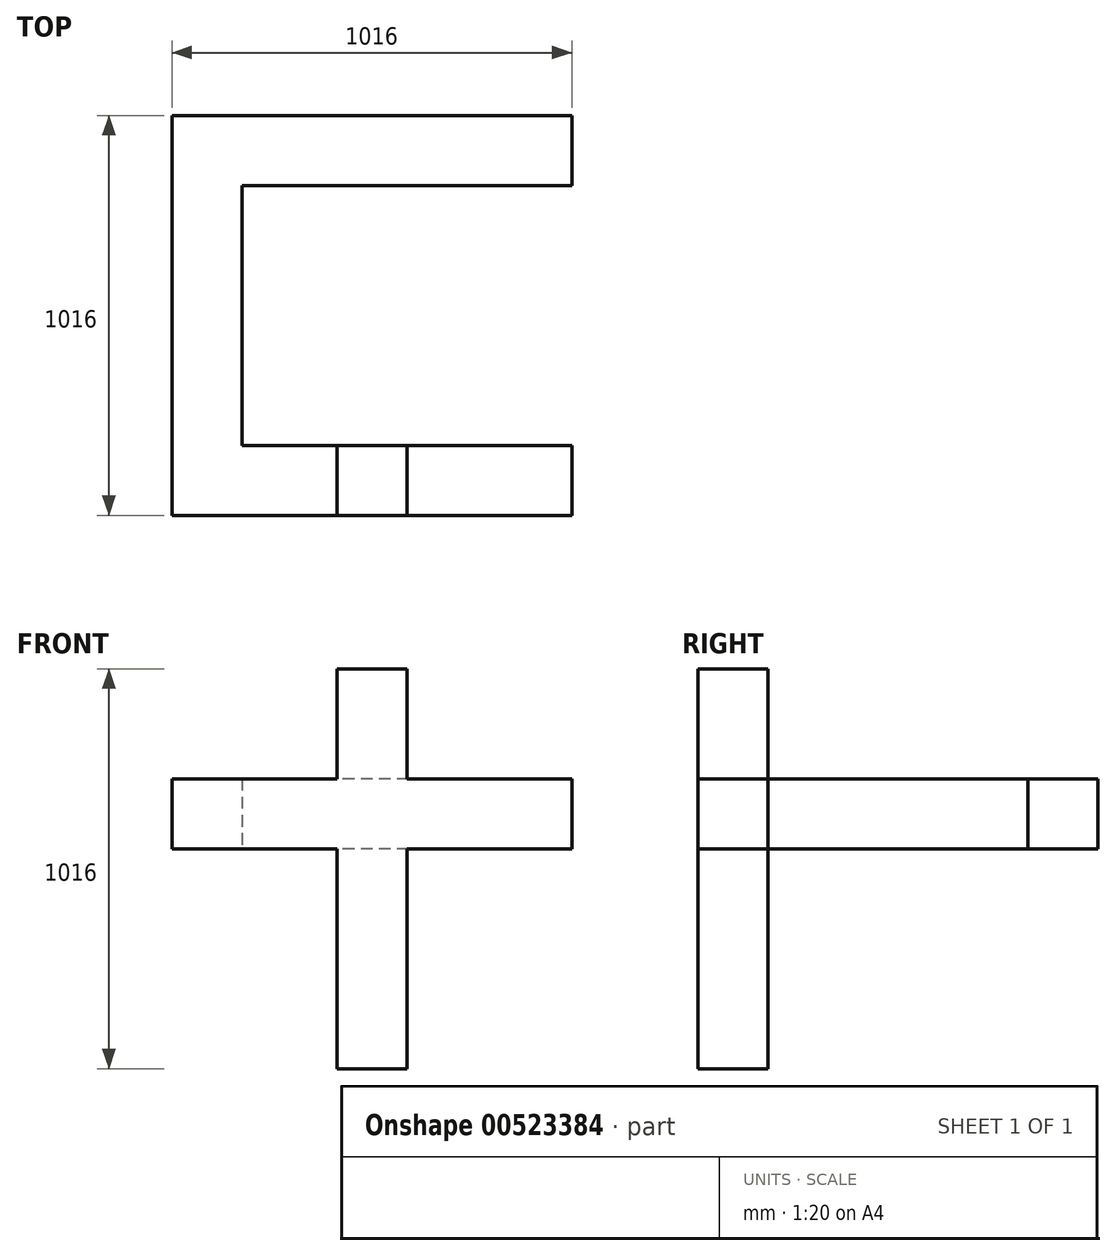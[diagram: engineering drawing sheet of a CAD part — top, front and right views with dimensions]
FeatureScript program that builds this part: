
annotation { "Feature Type Name" : "Feature", "Feature Type Description" : "" }
export const myFeature = defineFeature(function(context is Context, id is Id, definition is map)
    precondition{}
    {
        {
            var Q0;
            Q0=qCreatedBy(makeId("Top.planeOp"),FACE);
            var sketch = newSketch(context, id + "F0", { "sketchPlane" : qUnion([Q0])});
            skLineSegment(sketch, "E0.bottom", {"start": v(508, 508) * mm, "end": v(-508, 508) * mm});
            skLineSegment(sketch, "E0.top", {"start": v(508, -508) * mm, "end": v(-508, -508) * mm});
            skLineSegment(sketch, "E0.left", {"start": v(508, 508) * mm, "end": v(508, -508) * mm});
            skLineSegment(sketch, "E0.right", {"start": v(-508, 508) * mm, "end": v(-508, -508) * mm});
            skPoint(sketch, "E0.middle", {"position": v(0, 0) * mm});
            skLineSegment(sketch, "E1", {"start": v(508, 330.2) * mm, "end": v(-330.2, 330.2) * mm});
            skLineSegment(sketch, "E2", {"start": v(-330.2, 330.2) * mm, "end": v(-330.2, -330.2) * mm});
            skLineSegment(sketch, "E3", {"start": v(-330.2, -330.2) * mm, "end": v(508, -330.2) * mm});
            skSolve(sketch);
        }
        {
            var Q0;
            {var subQ3=sQuery(id+"F0.wireOp",EDGE,"E0.bottom");Q0=makeQuery(id+"F0.imprint","IMPRINT",FACE,{"disambiguationData":[TD([[makeQuery(id+"F0.imprint","IMPRINT",EDGE,{"derivedFrom":subQ3}),1.0]])]});}
            extrude(context, id + "F1", {"entities" : qUnion([Q0]), "depth" : 177.8 * mm, "offsetDistance" : 25.4 * mm});
        }
        {
            var Q0;
            Q0=makeQuery(id+"F1.opExtrude","SWEPT_FACE",FACE,{"disambiguationData":[OSD([sQuery(id+"F0.wireOp",EDGE,"E0.top")])]});
            var sketch = newSketch(context, id + "F2", { "sketchPlane" : qUnion([Q0])});
            skLineSegment(sketch, "E4.bottom", {"start": v(-88.9, 0) * mm, "end": v(88.9, 0) * mm});
            skLineSegment(sketch, "E4.top", {"start": v(-88.9, -558.8) * mm, "end": v(88.9, -558.8) * mm});
            skLineSegment(sketch, "E4.left", {"start": v(-88.9, 0) * mm, "end": v(-88.9, -558.8) * mm});
            skLineSegment(sketch, "E4.right", {"start": v(88.9, 0) * mm, "end": v(88.9, -558.8) * mm});
            skLineSegment(sketch, "E5.bottom", {"start": v(-88.9, 177.8) * mm, "end": v(88.9, 177.8) * mm});
            skLineSegment(sketch, "E5.top", {"start": v(-88.9, 457.2) * mm, "end": v(88.9, 457.2) * mm});
            skLineSegment(sketch, "E5.left", {"start": v(-88.9, 177.8) * mm, "end": v(-88.9, 457.2) * mm});
            skLineSegment(sketch, "E5.right", {"start": v(88.9, 177.8) * mm, "end": v(88.9, 457.2) * mm});
            skSolve(sketch);
        }
        {
            var Q0;
            Q0=makeQuery(id+"F2.imprint","IMPRINT",FACE,{"disambiguationData":[TD([[makeQuery(id+"F2.imprint","IMPRINT",EDGE,{"derivedFrom":sQuery(id+"F2.wireOp",EDGE,"E5.bottom")}),-1.0]])]});
            var Q1;
            Q1=makeQuery(id+"F2.imprint","IMPRINT",FACE,{"disambiguationData":[TD([[makeQuery(id+"F2.imprint","IMPRINT",EDGE,{"derivedFrom":sQuery(id+"F2.wireOp",EDGE,"E4.bottom")}),1.0]])]});
            extrude(context, id + "F3", {"entities" : qUnion([Q0, Q1]), "operationType" : NewBodyOperationType.ADD, "oppositeDirection" : true, "depth" : 177.8 * mm, "offsetDistance" : 25.4 * mm});
        }
    });
